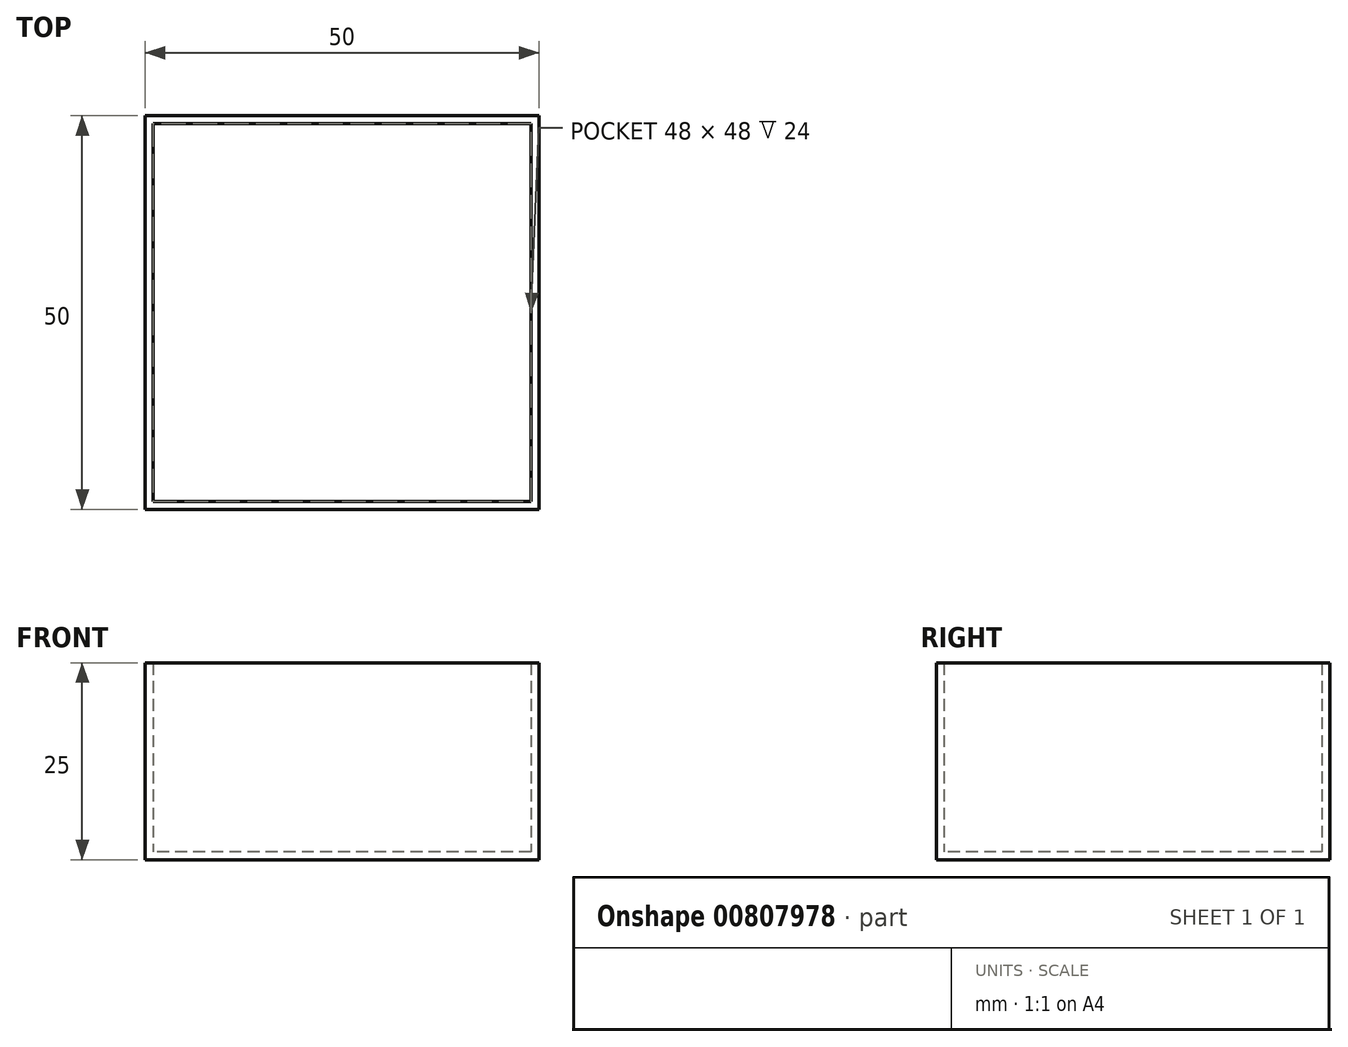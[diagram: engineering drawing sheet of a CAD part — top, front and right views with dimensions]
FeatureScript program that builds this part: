
annotation { "Feature Type Name" : "Feature", "Feature Type Description" : "" }
export const myFeature = defineFeature(function(context is Context, id is Id, definition is map)
    precondition{}
    {
        {
            var Q0;
            Q0=qCreatedBy(makeId("Top.planeOp"),FACE);
            var sketch = newSketch(context, id + "F0", { "sketchPlane" : qUnion([Q0])});
            skLineSegment(sketch, "E0.bottom", {"start": v(25, 25) * mm, "end": v(-25, 25) * mm});
            skLineSegment(sketch, "E0.top", {"start": v(25, -25) * mm, "end": v(-25, -25) * mm});
            skLineSegment(sketch, "E0.left", {"start": v(25, 25) * mm, "end": v(25, -25) * mm});
            skLineSegment(sketch, "E0.right", {"start": v(-25, 25) * mm, "end": v(-25, -25) * mm});
            skPoint(sketch, "E0.middle", {"position": v(0, 0) * mm});
            skSolve(sketch);
        }
        {
            var Q0;
            Q0=makeQuery(id+"F0.imprint","IMPRINT",FACE,{"disambiguationData":[TD([[makeQuery(id+"F0.imprint","IMPRINT",EDGE,{"derivedFrom":sQuery(id+"F0.wireOp",EDGE,"E0.bottom")}),1.0]])]});
            var sketch = newSketch(context, id + "F1", { "sketchPlane" : qUnion([Q0])});
            skSolve(sketch);
        }
        {
            var Q0;
            Q0=makeQuery(id+"F1.imprint","IMPRINT",FACE,{"disambiguationData":[TD([[makeQuery(id+"F1.imprint","IMPRINT",EDGE,{"derivedFrom":makeQuery(id+"F0.imprint","IMPRINT",EDGE,{"derivedFrom":sQuery(id+"F0.wireOp",EDGE,"E0.bottom")})}),1.0]])]});
            extrude(context, id + "F2", {"entities" : qUnion([Q0]), "depth" : 25 * mm, "offsetDistance" : 25 * mm});
        }
        {
            var Q0;
            Q0=makeQuery(id+"F2.opExtrude","CAP_FACE",FACE,{"disambiguationData":[OSD([sQuery(id+"F0.wireOp",EDGE,"E0.bottom"),sQuery(id+"F0.wireOp",EDGE,"E0.top"),sQuery(id+"F0.wireOp",EDGE,"E0.left"),sQuery(id+"F0.wireOp",EDGE,"E0.right")])],"isStart":false});
            shell(context, id + "F3", {"entities" : qUnion([Q0]), "thickness" : 1 * mm});
        }
    });
